# Revit family: v-273bzl5-ms_60Hz
name_source: partatom
category: 機械設備
units: mm (PartAtom-declared; Revit-internal decimal feet)

## family parameters
OmniClass タイトル = Centrifugal Fans
OmniClass 番号 = 23.75.35.17.27
パーツ タイプ = 標準
ロード時にボイドで切り取り = いいえ
丸型コネクタ寸法 = 直径を使用
作業面ベース = いいえ
共有 = いいえ
常に垂直 = はい
部屋計算ポイント = はい

## types (1)
- V-273BZL5-MS
    D1 = 610  [stored 2.00131 ft]
    Depth = 500  [stored 1.64042 ft]
    Duct_Depth = 114  [stored 0.374016 ft]
    Duct_EA_W = 143
    Duct_H = 96
    Duct_RA_W1 = 11  [stored 0.0360892 ft]
    Duct_RA_W2 = 65  [stored 0.213255 ft]
    EAサイズ_D = 98  [stored 0.321522 ft]
    H1 = 50  [stored 0.164042 ft]
    Height = 220  [stored 0.721785 ft]
    IfcExportAs = IfcFanType
    IfcExportType = PROPELLORAXIAL
    MAX静圧 = 0.0 Pa
    MAX風量 = 190.0 m³/h
    MID静圧 = 0.0 Pa
    MID風量 = 0.0 m³/h
    MIN静圧 = 0.0 Pa
    MIN風量 = 95.0 m³/h
    OmniClassCode = 23-33 31 19 11 15
    RAサイズ_D = 98  [stored 0.321522 ft]
    RAダクト接続口_A = はい
    RAダクト接続口_B = はい
    RAダクト接続口_C = いいえ
    URL = https://www.mitsubishielectric.co.jp
    Uniclass2015Code = Pr_65_67_29_12
    Uniclass2015Title = Centrifugal fans
    Uniclass2015Version = Systems v1.9
    W1 = 544  [stored 1.78478 ft]
    Width = 450  [stored 1.47638 ft]
    カバーマテリアル = 合成樹脂(白)
    ダクト径 = 100 mm
    ドレン管_H = 130  [stored 0.426509 ft]
    ドレン管_W = 115  [stored 0.377297 ft]
    ドレン管径 = 22 mm
    マテリアル = 亜鉛メッキ鋼板
    モデル = V-273BZL5-MS
    仕様書バージョン = Version1.0
    企業コード = 108420
    価格 = 337600 $
    分類コード = 50052503100080
    加湿給水管径 = 22 mm
    周波数 = 60 Hz
    呼称 = 天井扇
    天吊金具_径 = 15  [stored 0.0492126 ft]
    天吊金具_高さ = 102
    天吊金具ピッチ1 = 500  [stored 1.64042 ft]
    天吊金具ピッチ2 = 390  [stored 1.27953 ft]
    極数 = 3
    法定耐用年数 = 10
    消費電力 = 2100 W
    点検口 = はい
    点検口_Depth = 450  [stored 1.47638 ft]
    点検口離隔 = 350  [stored 1.14829 ft]
    相 = 1
    積算_科目 = 2 換気設備
    給水管_H = 60  [stored 0.19685 ft]
    給水管_W = 115  [stored 0.377297 ft]
    製品リリース年月 = 2022年6月1日
    製品出荷対象 = 国内
    製品質量 = 26.50 kg
    製造元 = 三菱電機株式会社
    設置方法 = カセット形
    説明 = バス乾燥・暖房・換気システム ミスト機能付 3部屋用
    負荷分類 = 3_ファン類
    質量 = 31.80 kg
    運転質量 = 0.00 kg
    電動機出力 = 0 W
    電圧 = 200 V

note: [stored X ft] marks values corroborated as IEEE doubles in the binary element streams (Revit-internal decimal feet)
